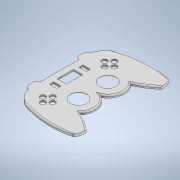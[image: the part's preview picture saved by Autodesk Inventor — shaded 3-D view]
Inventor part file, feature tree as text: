
AUTODESK INVENTOR PART (.ipt)
format: ipt  version: 2022 (Build 260153000, 153)  size: 488,448 bytes
history: native  units: mm
features: sketch x4, extrude x3, fillet x2
ambient origin geometry x8: Origin, YZ Plane, XZ Plane, XY Plane, X Axis, Y Axis, Z Axis, Center Point
bodies: Solid1 (feature_tree)
feature tree (9):
  sketch  "Sketch1"  dims[d0=35.0mm d1=60.0mm]
  extrude  "Extrusion1"  Depth=60.0mm
  extrude  "Extrusion2"  Depth=25.0mm
  extrude  "Extrusion4"  Depth=25.0mm
  fillet  "Fillet3"  Radius=27.0mm
  fillet  "Fillet4"  Radius=34.0mm
  sketch  "Sketch2"  dims[d2=17.5mm d3=25.0mm]
  sketch  "Sketch4"  dims[d4=22.5mm d6=25.0mm d7=27.0mm d8=34.0mm]
  sketch  "Sketch6"  dims[d9=27.0mm d10=7.5mm d11=25.0mm d12=27.0mm d13=34.0mm d14=27.0mm d15=6.0mm d16=6.0mm d17=6.0mm d18=6.5mm d22=6.0mm d23=40.0mm d25=360.0deg d27=25.0mm d28=27.0mm d31=40.0mm d32=25.0mm d33=27.0mm d34=5.0mm d35=8.0mm d36=8.0mm d58=40.0mm d60=360.0deg d62=50.0mm d63=2.0mm d64=0.0mm d70=13.425896mm d72=37.3mm d73=4.0mm d74=37.3mm d86=6.5mm d93=0.5mm d95=40.0mm d97=40.0mm d98=2.0mm d99=0.0mm d104=15.0mm d105=15.0mm d106=15.0mm d107=15.0mm d108=30.0mm d109=25.0mm d110=22.75mm d111=0.25mm d113=25.0mm d114=5.0mm d115=5.0mm d116=2.5mm d117=5.0mm d118=5.0mm d119=40.0mm d121=360.0deg d123=22.5mm d124=1.5mm d125=8.0mm d126=12.5mm d127=14.0mm d128=25.0mm d129=8.0mm d130=8.0mm d131=8.0mm d132=8.0mm d133=5.0mm d134=0.0mm d135=7.0mm d136=1.5mm d137=6.0mm d139=6.5mm d140=11.0mm d141=2.0mm d142=2.0mm]
